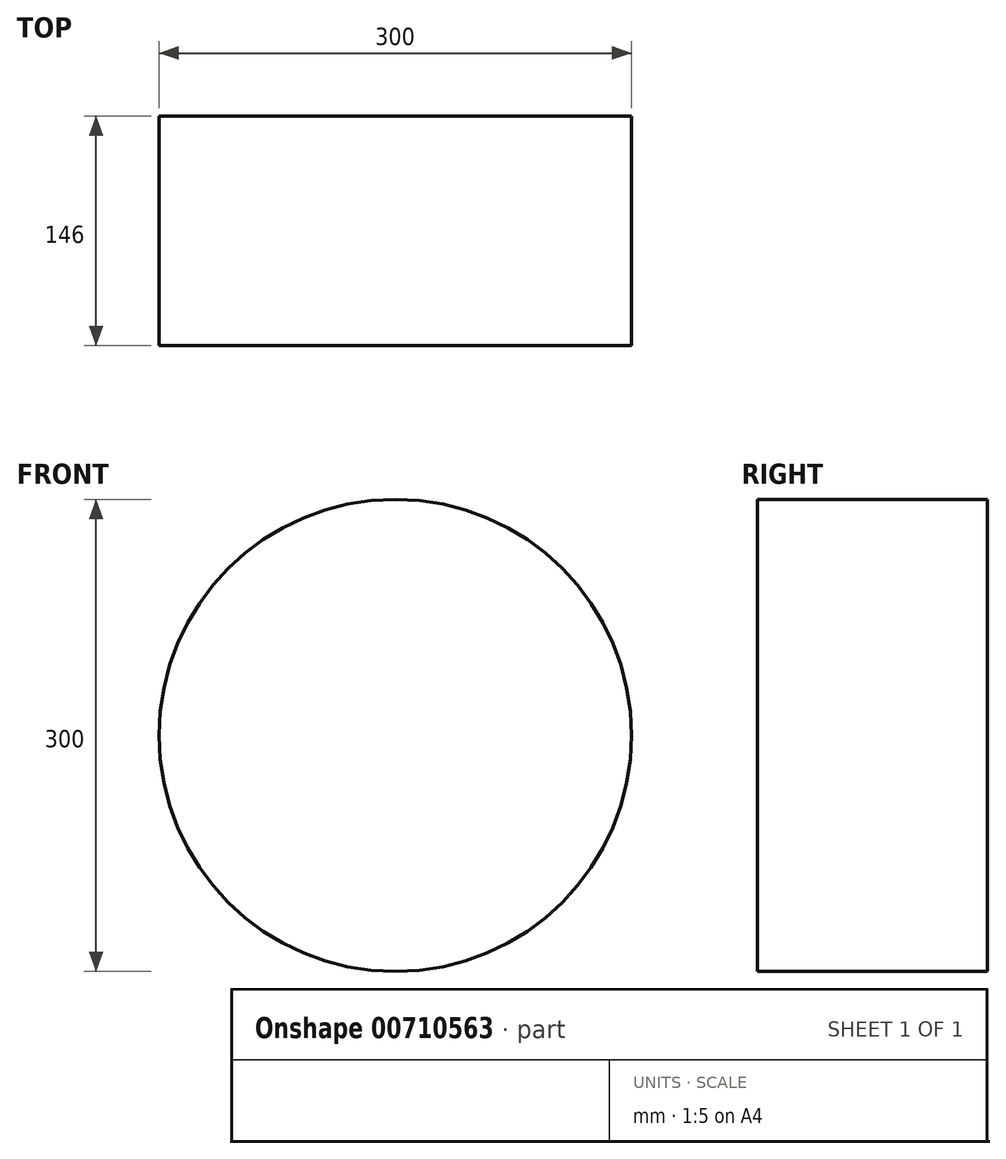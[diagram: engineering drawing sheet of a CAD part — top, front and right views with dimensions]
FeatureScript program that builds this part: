
annotation { "Feature Type Name" : "Feature", "Feature Type Description" : "" }
export const myFeature = defineFeature(function(context is Context, id is Id, definition is map)
    precondition{}
    {
        {
            var Q0;
            Q0=qCreatedBy(makeId("Front.planeOp"),FACE);
            var sketch = newSketch(context, id + "F0", { "sketchPlane" : qUnion([Q0])});
            skLineSegment(sketch, "E0", {"start": v(-249.43, 135.2) * mm, "end": v(-2.7, -96.02) * mm});
            skCircle(sketch, "E1", {"center": v(99.87, 13.43) * mm, "radius": 150 * mm});
            skPoint(sketch, "E1.second.point", {"position": v(200.96, 124.25) * mm});
            skPoint(sketch, "E1.third.point", {"position": v(71.66, 160.75) * mm});
            skLineSegment(sketch, "E2", {"start": v(6.07, -135.76) * mm, "end": v(284.53, -138.18) * mm});
            skLineSegment(sketch, "E3", {"start": v(-274.32, 127) * mm, "end": v(6.07, -135.76) * mm});
            skSolve(sketch);
        }
        {
            var Q0;
            {var subQ0=sQuery(id+"F0.wireOp",EDGE,"E1");Q0=makeQuery(id+"F0.imprint","IMPRINT",FACE,{"disambiguationData":[TD([[makeQuery(id+"F0.imprint","IMPRINT",EDGE,{"disambiguationData":[TD([[makeQuery(id+"F0.imprint","IMPRINT",VERTEX,{"derivedFrom":subQ0}),-1.0]])],"derivedFrom":subQ0}),1.0]])]});}
            extrude(context, id + "F1", {"entities" : qUnion([Q0]), "depth" : 146 * mm, "offsetDistance" : 25 * mm});
        }
    });
